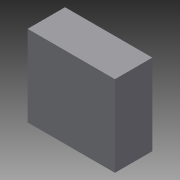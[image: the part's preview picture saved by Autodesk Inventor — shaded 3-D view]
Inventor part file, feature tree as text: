
AUTODESK INVENTOR PART (.ipt)
format: ipt  version: 2013 (Build 170138000, 138)  size: 66,048 bytes
history: native  units: in
note: dims shown in document units (in); Inventor stores cm internally (conversion verified against a paired STEP export)
features: extrude x1, sketch x1
ambient origin geometry x8: Origin, YZ Plane, XZ Plane, XY Plane, X Axis, Y Axis, Z Axis, Center Point
bodies: Solid1 (feature_tree)
feature tree (2):
  extrude  "Extrusion1"  Depth=3.0in
  sketch  "Sketch1"  dims[d0=7.0in d1=3.0in d2=6.5in d3=0.0in]
